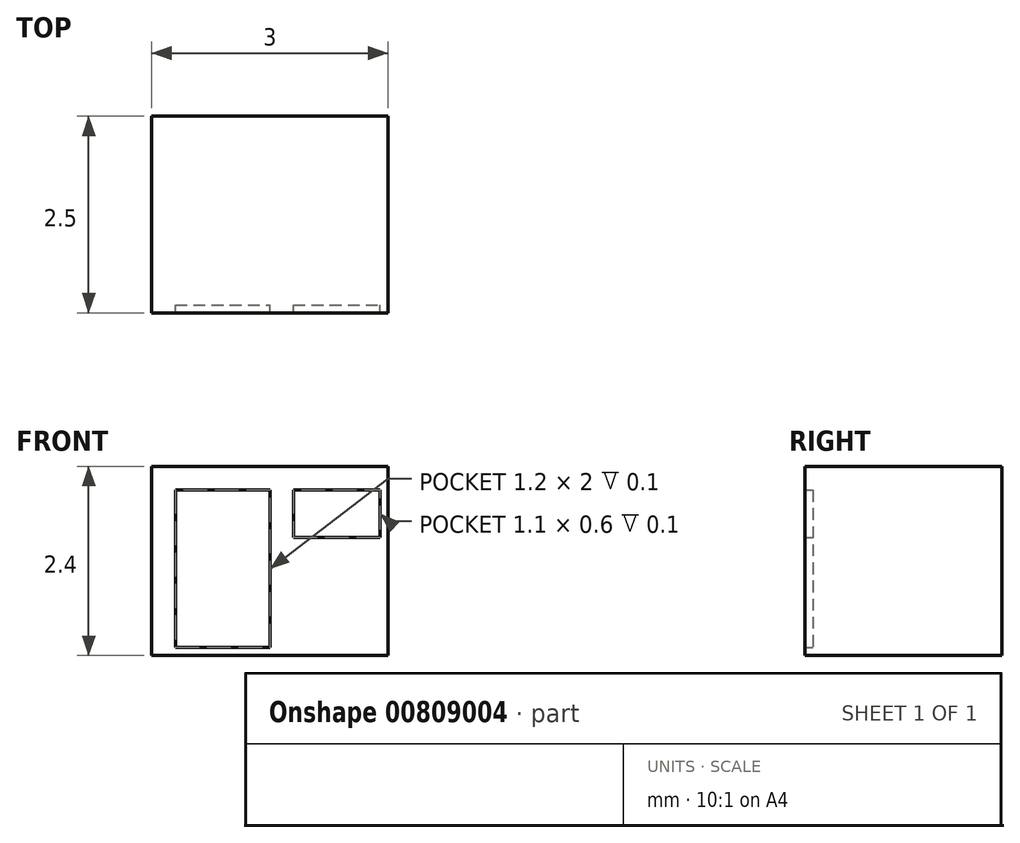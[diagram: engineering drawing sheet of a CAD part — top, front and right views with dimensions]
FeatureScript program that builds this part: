
annotation { "Feature Type Name" : "Feature", "Feature Type Description" : "" }
export const myFeature = defineFeature(function(context is Context, id is Id, definition is map)
    precondition{}
    {
        {
            var Q0;
            Q0=qCreatedBy(makeId("Front.planeOp"),FACE);
            var sketch = newSketch(context, id + "F0", { "sketchPlane" : qUnion([Q0])});
            skLineSegment(sketch, "E0.bottom", {"start": v(1.5, -1.2) * mm, "end": v(-1.5, -1.2) * mm});
            skLineSegment(sketch, "E0.top", {"start": v(1.5, 1.2) * mm, "end": v(-1.5, 1.2) * mm});
            skLineSegment(sketch, "E0.left", {"start": v(1.5, -1.2) * mm, "end": v(1.5, 1.2) * mm});
            skLineSegment(sketch, "E0.right", {"start": v(-1.5, -1.2) * mm, "end": v(-1.5, 1.2) * mm});
            skPoint(sketch, "E0.middle", {"position": v(0, 0) * mm});
            skLineSegment(sketch, "E1.bottom", {"start": v(-1.2, 0.9) * mm, "end": v(0, 0.9) * mm});
            skLineSegment(sketch, "E1.top", {"start": v(-1.2, -1.1) * mm, "end": v(0, -1.1) * mm});
            skLineSegment(sketch, "E1.left", {"start": v(-1.2, 0.9) * mm, "end": v(-1.2, -1.1) * mm});
            skLineSegment(sketch, "E1.right", {"start": v(0, 0.9) * mm, "end": v(0, -1.1) * mm});
            skLineSegment(sketch, "E2.bottom", {"start": v(0.3, 0.9) * mm, "end": v(1.4, 0.9) * mm});
            skLineSegment(sketch, "E2.top", {"start": v(0.3, 0.3) * mm, "end": v(1.4, 0.3) * mm});
            skLineSegment(sketch, "E2.left", {"start": v(0.3, 0.9) * mm, "end": v(0.3, 0.3) * mm});
            skLineSegment(sketch, "E2.right", {"start": v(1.4, 0.9) * mm, "end": v(1.4, 0.3) * mm});
            skSolve(sketch);
        }
        {
            var Q0;
            Q0=makeQuery(id+"F0.imprint","IMPRINT",FACE,{"disambiguationData":[TD([[makeQuery(id+"F0.imprint","IMPRINT",EDGE,{"derivedFrom":sQuery(id+"F0.wireOp",EDGE,"E0.bottom")}),-1.0]])]});
            extrude(context, id + "F1", {"entities" : qUnion([Q0]), "depth" : .1 * mm, "offsetDistance" : 25 * mm});
        }
        {
            var Q0;
            Q0 = qSketchRegion(id + "F0", true);
            var Q1;
            Q1=makeQuery(id+"F0.imprint","IMPRINT",FACE,{"disambiguationData":[TD([[makeQuery(id+"F0.imprint","IMPRINT",EDGE,{"derivedFrom":sQuery(id+"F0.wireOp",EDGE,"E1.bottom")}),-1.0]])]});
            var Q2;
            Q2=makeQuery(id+"F0.imprint","IMPRINT",FACE,{"disambiguationData":[TD([[makeQuery(id+"F0.imprint","IMPRINT",EDGE,{"derivedFrom":sQuery(id+"F0.wireOp",EDGE,"E2.bottom")}),-1.0]])]});
            extrude(context, id + "F2", {"entities" : qUnion([Q0, Q1, Q2]), "operationType" : NewBodyOperationType.ADD, "oppositeDirection" : true, "depth" : 2.4 * mm, "offsetDistance" : 25 * mm});
        }
    });
